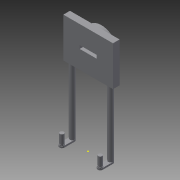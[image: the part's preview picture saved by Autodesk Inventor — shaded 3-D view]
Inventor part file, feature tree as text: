
AUTODESK INVENTOR PART (.ipt)
format: ipt  version: 2015 SP2 (Build 190223200, 223)  size: 162,304 bytes
history: native  units: mm
features: sketch x10, extrude x9
ambient origin geometry x8: Origin, YZ Plane, XZ Plane, XY Plane, X Axis, Y Axis, Z Axis, Center Point
bodies: Solid1 (feature_tree)
feature tree (19):
  sketch  "Sketch1"  dims[d0=5.1mm d1=1.0mm]
  sketch  "Sketch2"  dims[d2=15.0mm d3=12.0mm]
  extrude  "Extrusion1"  Depth=1.0mm
  extrude  "Extrusion2"  Depth=12.0mm
  extrude  "Extrusion4"  Depth=2.0mm TaperAngle=0.0deg
  extrude  "Extrusion5"  Depth=4.0mm TaperAngle=0.0deg
  extrude  "Extrusion6"  Depth=5.1mm
  extrude  "Extrusion7"  Depth=3.0mm TaperAngle=0.0deg
  extrude  "Extrusion8"  Depth=20.0mm TaperAngle=0.0deg
  sketch  "Sketch15"  dims[d25=1.5mm d26=1.5mm]
  extrude  "Extrusion9"  Depth=1.5mm
  extrude  "Extrusion10"  Depth=0.5mm
  sketch  "Sketch3"  dims[d4=10.0mm d5=2.0mm d6=0.0mm]
  sketch  "Sketch7"  dims[d7=2.0mm d8=0.0mm d11=4.0mm d12=0.0mm]
  sketch  "Sketch8"  dims[d13=3.0mm d14=0.0mm d15=5.1mm]
  sketch  "Sketch9"  dims[d16=1.0mm d17=3.0mm d18=0.0mm]
  sketch  "Sketch14"  dims[d19=1.5mm d20=20.0mm d21=0.0mm]
  sketch  "Sketch17"  dims[d27=0.5mm d28=0.0mm d29=1.2mm]
  sketch  "Sketch19"  dims[d30=3.0mm d31=0.0mm d32=1.35mm d33=1.35mm d34=1.35mm d35=1.35mm d36=0.25mm d37=0.0mm]
